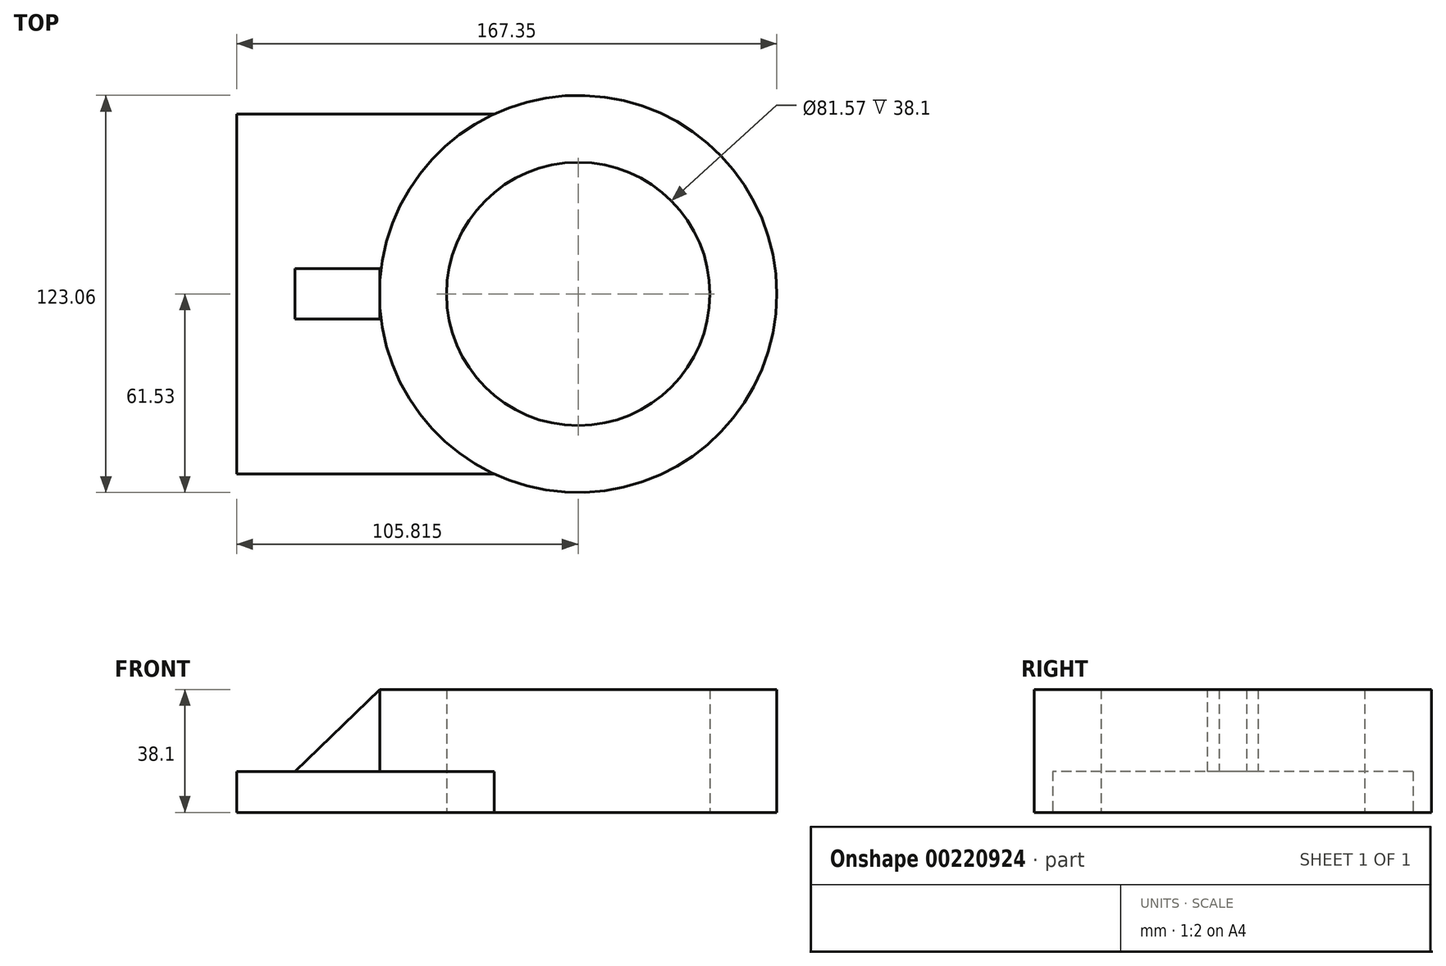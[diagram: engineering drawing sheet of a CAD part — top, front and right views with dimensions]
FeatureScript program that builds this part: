
annotation { "Feature Type Name" : "Feature", "Feature Type Description" : "" }
export const myFeature = defineFeature(function(context is Context, id is Id, definition is map)
    precondition{}
    {
        {
            var Q0;
            Q0=qCreatedBy(makeId("Top.planeOp"),FACE);
            var sketch = newSketch(context, id + "F0", { "sketchPlane" : qUnion([Q0])});
            skLineSegment(sketch, "E0.bottom", {"start": v(-80.1, 55.77) * mm, "end": v(0.48, 55.77) * mm});
            skLineSegment(sketch, "E0.top", {"start": v(-80.1, -55.77) * mm, "end": v(0.48, -55.77) * mm});
            skLineSegment(sketch, "E0.left", {"start": v(-80.1, 55.77) * mm, "end": v(-80.1, -55.77) * mm});
            skPoint(sketch, "E0.middle", {"position": v(-39.81, 0) * mm});
            skCircle(sketch, "E1", {"center": v(25.7, 0) * mm, "radius": 61.53 * mm});
            skCircle(sketch, "E2", {"center": v(25.7, 0) * mm, "radius": 40.79 * mm});
            skSolve(sketch);
        }
        {
            var Q0;
            {var subQ0=sQuery(id+"F0.wireOp",EDGE,"E0.left");Q0=makeQuery(id+"F0.imprint","IMPRINT",FACE,{"disambiguationData":[TD([[makeQuery(id+"F0.imprint","IMPRINT",EDGE,{"derivedFrom":subQ0}),1.0]])]});}
            extrude(context, id + "F1", {"entities" : qUnion([Q0]), "depth" : 12.7 * mm});
        }
        {
            var Q0;
            Q0=makeQuery(id+"F0.imprint","IMPRINT",FACE,{"disambiguationData":[TD([[makeQuery(id+"F0.imprint","IMPRINT",EDGE,{"derivedFrom":sQuery(id+"F0.wireOp",EDGE,"E2")}),-1.0]])]});
            extrude(context, id + "F2", {"entities" : qUnion([Q0]), "operationType" : NewBodyOperationType.ADD, "depth" : 38.1 * mm});
        }
        {
            var Q0;
            Q0=makeQuery(id+"F1.opExtrude","CAP_FACE",FACE,{"disambiguationData":[OSD([sQuery(id+"F0.wireOp",EDGE,"E0.bottom"),sQuery(id+"F0.wireOp",EDGE,"E0.top"),sQuery(id+"F0.wireOp",EDGE,"E0.left"),sQuery(id+"F0.wireOp",EDGE,"E1")])],"isStart":false});
            var sketch = newSketch(context, id + "F3", { "sketchPlane" : qUnion([Q0])});
            skLineSegment(sketch, "E3.bottom", {"start": v(-62.07, 7.8) * mm, "end": v(-35.68, 7.8) * mm});
            skLineSegment(sketch, "E3.top", {"start": v(-62.07, -7.8) * mm, "end": v(-35.68, -7.8) * mm});
            skLineSegment(sketch, "E3.left", {"start": v(-62.07, 7.8) * mm, "end": v(-62.07, -7.8) * mm});
            skLineSegment(sketch, "E3.right", {"start": v(-35.68, 7.8) * mm, "end": v(-35.68, -7.8) * mm});
            skPoint(sketch, "E3.middle", {"position": v(-48.88, 0) * mm});
            skSolve(sketch);
        }
        {
            var Q0;
            {var subQ1=sQuery(id+"F3.wireOp",EDGE,"E3.bottom");Q0=makeQuery(id+"F3.imprint","IMPRINT",FACE,{"disambiguationData":[TD([[makeQuery(id+"F3.imprint","IMPRINT",EDGE,{"derivedFrom":subQ1}),-1.0]])]});}
            extrude(context, id + "F4", {"entities" : qUnion([Q0]), "operationType" : NewBodyOperationType.ADD, "depth" : 25.4 * mm});
        }
        {
            var Q0;
            Q0=makeQuery(id+"F4.opExtrude","SWEPT_FACE",FACE,{"disambiguationData":[OSD([sQuery(id+"F3.wireOp",EDGE,"E3.top")])]});
            var sketch = newSketch(context, id + "F5", { "sketchPlane" : qUnion([Q0])});
            skLineSegment(sketch, "E4", {"start": v(-62.07, 12.7) * mm, "end": v(-35.68, 38.1) * mm});
            skSolve(sketch);
        }
        {
            var Q0;
            Q0=makeQuery(id+"F5.imprint","IMPRINT",FACE,{"disambiguationData":[TD([[makeQuery(id+"F5.imprint","IMPRINT",EDGE,{"derivedFrom":sQuery(id+"F5.wireOp",EDGE,"E4")}),1.0]])]});
            extrude(context, id + "F6", {"entities" : qUnion([Q0]), "operationType" : NewBodyOperationType.REMOVE, "endBound" : BoundingType.THROUGH_ALL, "oppositeDirection" : true, "depth" : 25.4 * mm});
        }
    });
